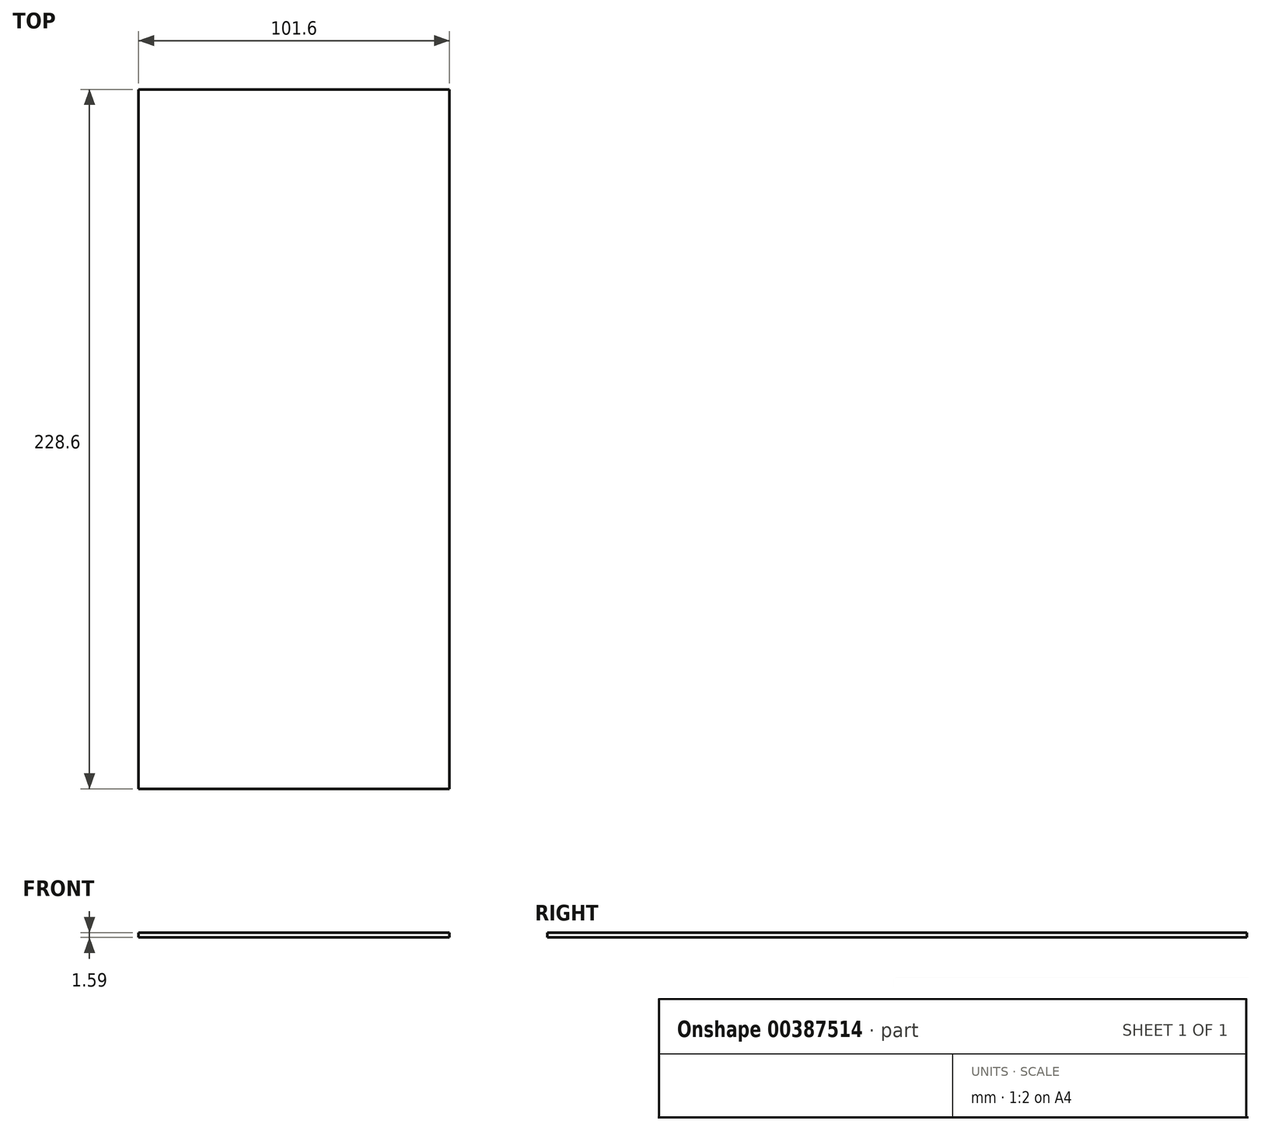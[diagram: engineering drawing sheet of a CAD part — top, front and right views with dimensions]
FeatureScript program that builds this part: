
annotation { "Feature Type Name" : "Feature", "Feature Type Description" : "" }
export const myFeature = defineFeature(function(context is Context, id is Id, definition is map)
    precondition{}
    {
        {
            var Q0;
            Q0=qCreatedBy(makeId("Top.planeOp"),FACE);
            var sketch = newSketch(context, id + "F0", { "sketchPlane" : qUnion([Q0])});
            skLineSegment(sketch, "E0.bottom", {"start": v(0, 0) * mm, "end": v(101.6, 0) * mm});
            skLineSegment(sketch, "E0.top", {"start": v(0, 228.6) * mm, "end": v(101.6, 228.6) * mm});
            skLineSegment(sketch, "E0.left", {"start": v(0, 0) * mm, "end": v(0, 228.6) * mm});
            skLineSegment(sketch, "E0.right", {"start": v(101.6, 0) * mm, "end": v(101.6, 228.6) * mm});
            skSolve(sketch);
        }
        {
            var Q0;
            Q0 = qSketchRegion(id + "F0", true);
            extrude(context, id + "F1", {"entities" : qUnion([Q0]), "depth" : 1.59 * mm});
        }
    });
